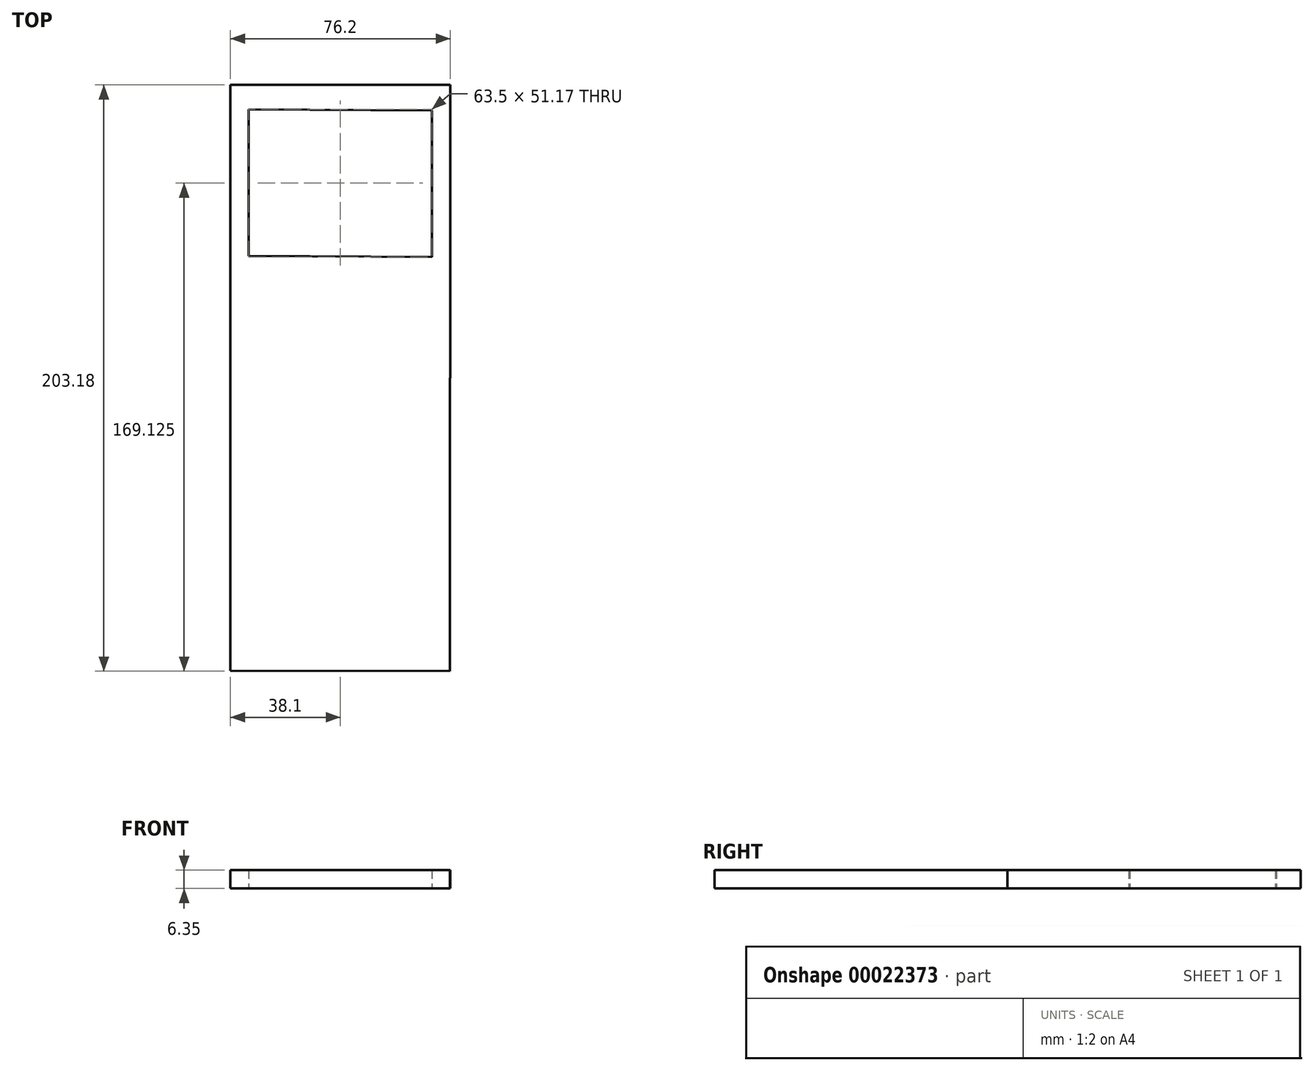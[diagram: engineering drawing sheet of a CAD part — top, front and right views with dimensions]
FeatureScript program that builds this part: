
annotation { "Feature Type Name" : "Feature", "Feature Type Description" : "" }
export const myFeature = defineFeature(function(context is Context, id is Id, definition is map)
    precondition{}
    {
        {
            var Q0;
            Q0=qCreatedBy(makeId("Top.planeOp"),FACE);
            var sketch = newSketch(context, id + "F0", { "sketchPlane" : qUnion([Q0])});
            skLineSegment(sketch, "E0", {"start": v(0, 0) * mm, "end": v(38.1, 0) * mm});
            skLineSegment(sketch, "E1", {"start": v(0, 0) * mm, "end": v(-38.1, 0) * mm});
            skLineSegment(sketch, "E2", {"start": v(-38.1, 0) * mm, "end": v(-38.1, 101.6) * mm});
            skLineSegment(sketch, "E3", {"start": v(38.1, -0.02) * mm, "end": v(38.1, 101.58) * mm});
            skLineSegment(sketch, "E4", {"start": v(37.95, -101.58) * mm, "end": v(37.95, 0.02) * mm});
            skLineSegment(sketch, "E5", {"start": v(-38.08, -101.45) * mm, "end": v(-38.08, 0.15) * mm});
            skLineSegment(sketch, "E6", {"start": v(-38.1, 101.6) * mm, "end": v(38.1, 101.58) * mm});
            skLineSegment(sketch, "E7", {"start": v(37.95, -101.58) * mm, "end": v(-38.08, -101.45) * mm});
            skLineSegment(sketch, "E8", {"start": v(-31.75, 93.13) * mm, "end": v(31.75, 92.76) * mm});
            skLineSegment(sketch, "E9", {"start": v(31.75, 92.76) * mm, "end": v(31.75, 41.96) * mm});
            skLineSegment(sketch, "E10", {"start": v(-31.75, 93.13) * mm, "end": v(-31.75, 42.33) * mm});
            skLineSegment(sketch, "E11", {"start": v(-31.75, 42.33) * mm, "end": v(31.75, 41.96) * mm});
            skSolve(sketch);
        }
        {
            var Q0;
            {var subQ0=sQuery(id+"F0.wireOp",EDGE,"E7");Q0=makeQuery(id+"F0.imprint","IMPRINT",FACE,{"disambiguationData":[TD([[makeQuery(id+"F0.imprint","IMPRINT",EDGE,{"derivedFrom":subQ0}),-1.0]])]});}
            var Q1;
            {var subQ4=sQuery(id+"F0.wireOp",EDGE,"E2");Q1=makeQuery(id+"F0.imprint","IMPRINT",FACE,{"disambiguationData":[TD([[makeQuery(id+"F0.imprint","IMPRINT",EDGE,{"derivedFrom":subQ4}),-1.0]])]});}
            extrude(context, id + "F1", {"entities" : qUnion([Q0, Q1]), "depth" : 6.35 * mm});
        }
    });
